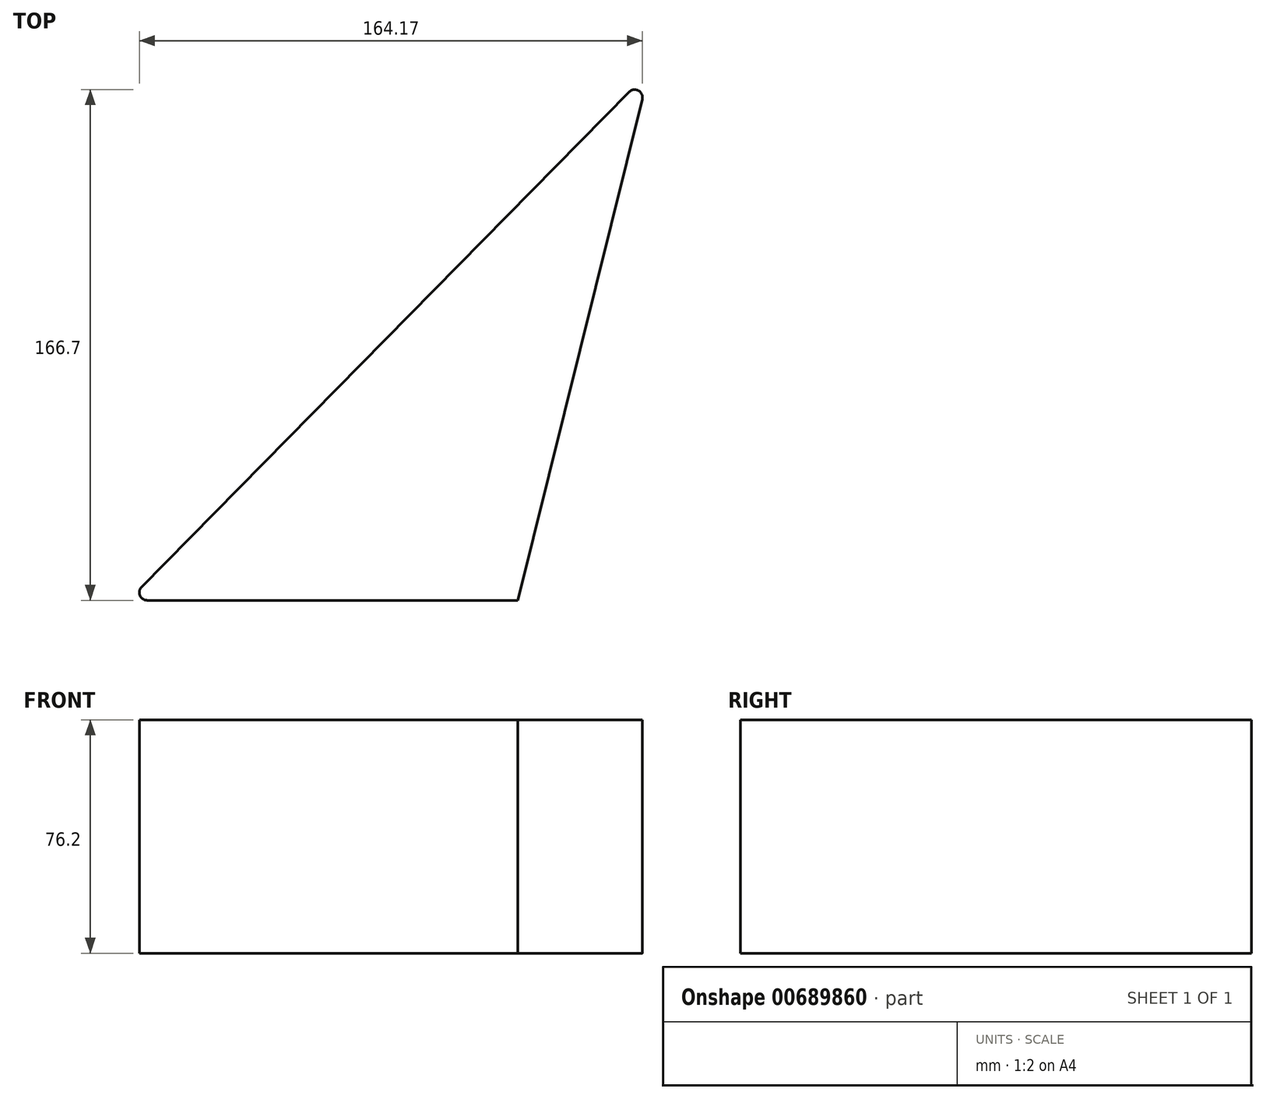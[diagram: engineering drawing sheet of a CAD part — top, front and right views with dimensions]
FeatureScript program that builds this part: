
annotation { "Feature Type Name" : "Feature", "Feature Type Description" : "" }
export const myFeature = defineFeature(function(context is Context, id is Id, definition is map)
    precondition{}
    {
        {
            var Q0;
            Q0=qCreatedBy(makeId("Top.planeOp"),FACE);
            var sketch = newSketch(context, id + "F0", { "sketchPlane" : qUnion([Q0])});
            skLineSegment(sketch, "E0", {"start": v(23.73, -42.97) * mm, "end": v(-103.27, -42.97) * mm});
            skLineSegment(sketch, "E1", {"start": v(-103.27, -42.97) * mm, "end": v(66.58, 129.59) * mm});
            skLineSegment(sketch, "E2", {"start": v(66.58, 129.59) * mm, "end": v(23.73, -42.97) * mm});
            skSolve(sketch);
        }
        {
            var Q0;
            Q0=makeQuery(id+"F0.imprint","IMPRINT",FACE,{"disambiguationData":[TD([[makeQuery(id+"F0.imprint","IMPRINT",EDGE,{"derivedFrom":sQuery(id+"F0.wireOp",EDGE,"E0")}),-1.0]])]});
            var Q1;
            Q1 = qConstructionFilter(qBodyType(qCreatedBy(id + "F0" ,EDGE), BodyType.WIRE), ConstructionObject.NO);
            extrude(context, id + "F1", {"entities" : qUnion([Q0]), "surfaceEntities" : qUnion([Q1]), "depth" : 76.2 * mm, "offsetDistance" : 25.4 * mm});
        }
        {
            var Q0;
            Q0=makeQuery(id+"F1.opExtrude","CAP_FACE",FACE,{"disambiguationData":[OSD([sQuery(id+"F0.wireOp",EDGE,"E0"),sQuery(id+"F0.wireOp",EDGE,"E1"),sQuery(id+"F0.wireOp",EDGE,"E2"),sQuery(id+"F0.wireOp",EDGE,"0fcb691d-4dca-40d9-bc82-fd5563c62b47.0"),sQuery(id+"F0.wireOp",EDGE,"0fcb691d-4dca-40d9-bc82-fd5563c62b47.1"),sQuery(id+"F0.wireOp",EDGE,"0fcb691d-4dca-40d9-bc82-fd5563c62b47.2")])],"isStart":true});
            var sketch = newSketch(context, id + "F2", { "sketchPlane" : qUnion([Q0])});
            skLineSegment(sketch, "E3", {"start": v(-103.27, 42.97) * mm, "end": v(23.73, 42.97) * mm});
            skLineSegment(sketch, "E4", {"start": v(23.73, 42.97) * mm, "end": v(66.58, -129.59) * mm});
            skLineSegment(sketch, "E5", {"start": v(66.58, -129.59) * mm, "end": v(-103.27, 42.97) * mm});
            skSolve(sketch);
        }
        {
            var Q0;
            Q0 = qSketchRegion(id + "F2", true);
            extrude(context, id + "F3", {"entities" : qUnion([Q0]), "operationType" : NewBodyOperationType.ADD, "oppositeDirection" : true, "depth" : 2 * mm, "offsetDistance" : 25.4 * mm});
        }
        {
            var Q0;
            Q0=makeQuery(id+"F1.opExtrude","SWEPT_EDGE",EDGE,{"disambiguationData":[OSD([sQuery(id+"F0.wireOp",EDGE,"E0"),sQuery(id+"F0.wireOp",EDGE,"E1")])]});
            var Q1;
            Q1=makeQuery(id+"F1.opExtrude","SWEPT_EDGE",EDGE,{"disambiguationData":[OSD([sQuery(id+"F0.wireOp",EDGE,"E1"),sQuery(id+"F0.wireOp",EDGE,"E2")])]});
            fillet(context, id + "F4", {"entities" : qUnion([Q0, Q1]), "radius" : 2.54 * mm, "tangentPropagation" : true, "allowEdgeOverflow" : false});
        }
    });
